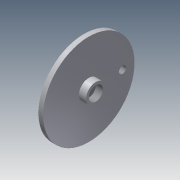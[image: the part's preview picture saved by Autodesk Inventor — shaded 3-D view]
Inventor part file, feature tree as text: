
AUTODESK INVENTOR PART (.ipt)
format: ipt  version: 2013 (Build 170138000, 138)  size: 97,280 bytes
history: native  units: mm
features: sketch x5, extrude x4
ambient origin geometry x8: Origin, YZ Plane, XZ Plane, XY Plane, X Axis, Y Axis, Z Axis, Center Point
bodies: Solid1 (feature_tree)
feature tree (9):
  extrude  "Extrusion1"  Depth=2.0mm TaperAngle=0.0deg
  extrude  "Extrusion2"  Depth=3.0mm TaperAngle=0.0deg
  sketch  "Sketch3"  dims[d7=6.0mm d8=3.0mm d9=0.0mm]
  extrude  "Extrusion3"  Depth=3.0mm TaperAngle=0.0deg
  extrude  "Extrusion4"  Depth=2.0mm TaperAngle=0.0deg
  sketch  "Sketch1"  dims[d0=38.6mm d2=2.0mm d3=0.0mm]
  sketch  "Sketch2"  dims[d4=8.4mm d5=3.0mm d6=0.0mm]
  sketch  "Sketch4"  dims[d11=3.0mm d12=2.0mm d13=0.0mm]
  sketch  "Sketch5"
